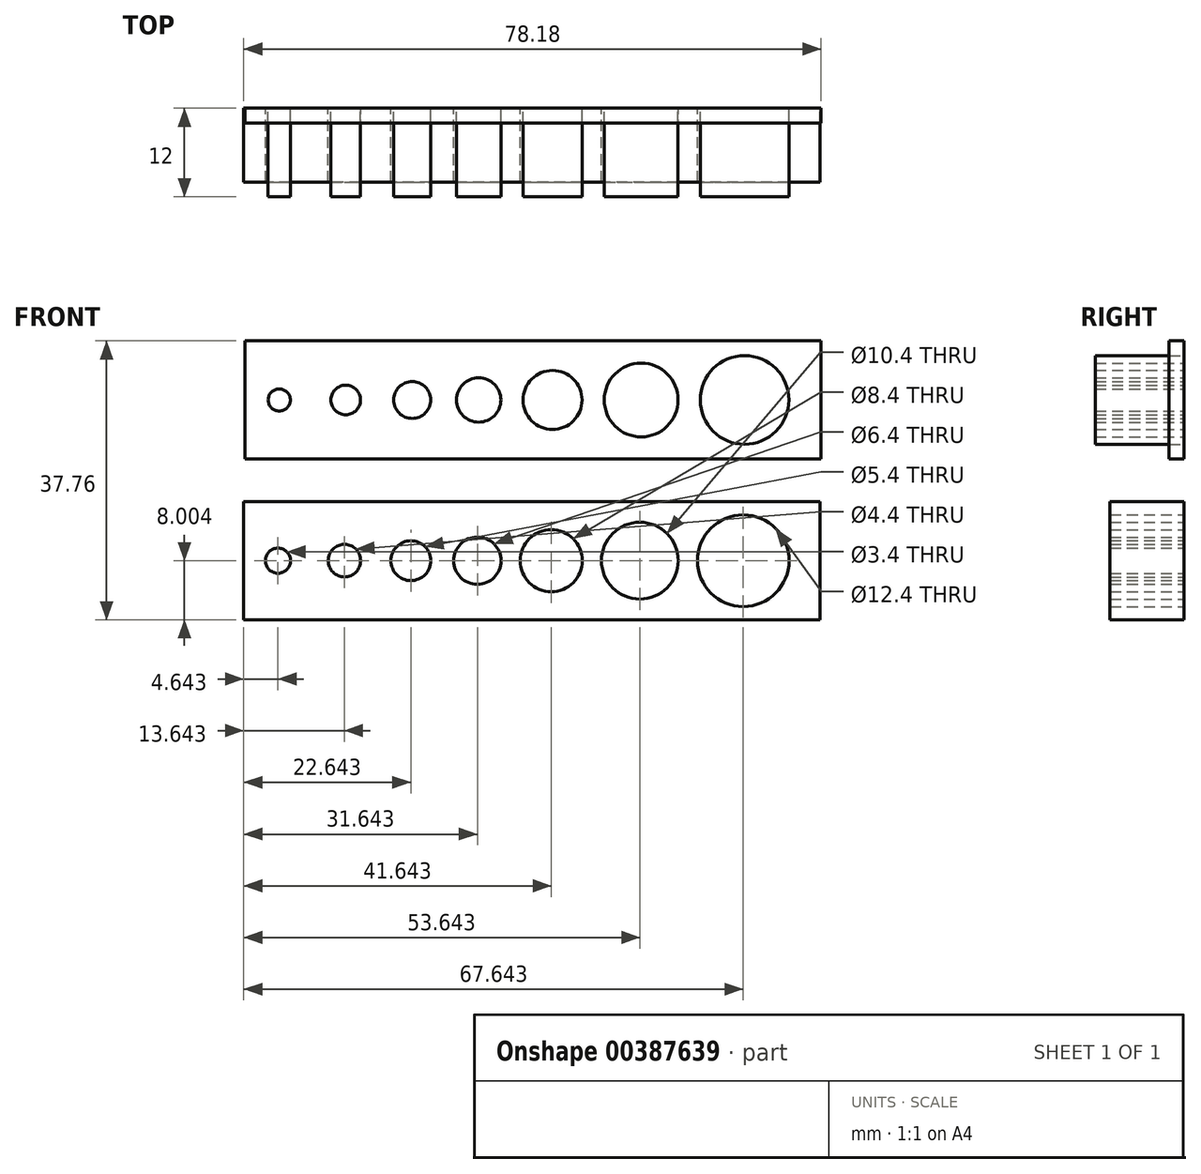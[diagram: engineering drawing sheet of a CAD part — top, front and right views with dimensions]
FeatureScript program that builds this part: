
annotation { "Feature Type Name" : "Feature", "Feature Type Description" : "" }
export const myFeature = defineFeature(function(context is Context, id is Id, definition is map)
    precondition{}
    {
        {
            var Q0;
            Q0=qCreatedBy(makeId("Front.planeOp"),FACE);
            var sketch = newSketch(context, id + "F0", { "sketchPlane" : qUnion([Q0])});
            skLineSegment(sketch, "E0", {"start": v(-39.38, 0) * mm, "end": v(47.78, 0) * mm, "construction": true});
            skCircle(sketch, "E1", {"center": v(-31.97, 0) * mm, "radius": 1.5 * mm});
            skCircle(sketch, "E2", {"center": v(-22.97, 0) * mm, "radius": 2 * mm});
            skCircle(sketch, "E3", {"center": v(-13.97, 0) * mm, "radius": 2.5 * mm});
            skCircle(sketch, "E4", {"center": v(-4.97, 0) * mm, "radius": 3 * mm});
            skCircle(sketch, "E5", {"center": v(5.03, 0) * mm, "radius": 4 * mm});
            skCircle(sketch, "E6", {"center": v(17.03, 0) * mm, "radius": 5 * mm});
            skCircle(sketch, "E7", {"center": v(31.03, 0) * mm, "radius": 6 * mm});
            skLineSegment(sketch, "E8.bottom", {"start": v(-36.6, -8) * mm, "end": v(41.4, -8) * mm});
            skLineSegment(sketch, "E8.top", {"start": v(-36.6, 8) * mm, "end": v(41.4, 8) * mm});
            skLineSegment(sketch, "E8.left", {"start": v(-36.6, -8) * mm, "end": v(-36.6, 8) * mm});
            skLineSegment(sketch, "E8.right", {"start": v(41.4, -8) * mm, "end": v(41.4, 8) * mm});
            skPoint(sketch, "E9", {"position": v(41.4, 0) * mm});
            skSolve(sketch);
        }
        {
            var Q0;
            Q0=qCreatedBy(makeId("Front.planeOp"),FACE);
            var sketch = newSketch(context, id + "F1", { "sketchPlane" : qUnion([Q0])});
            skLineSegment(sketch, "E10", {"start": v(-39.55, -21.76) * mm, "end": v(47.6, -21.76) * mm, "construction": true});
            skCircle(sketch, "E11", {"center": v(-32.15, -21.76) * mm, "radius": 1.7 * mm});
            skCircle(sketch, "E12", {"center": v(-23.15, -21.76) * mm, "radius": 2.2 * mm});
            skCircle(sketch, "E13", {"center": v(-14.15, -21.76) * mm, "radius": 2.7 * mm});
            skCircle(sketch, "E14", {"center": v(-5.15, -21.76) * mm, "radius": 3.2 * mm});
            skCircle(sketch, "E15", {"center": v(4.85, -21.76) * mm, "radius": 4.2 * mm});
            skCircle(sketch, "E16", {"center": v(16.85, -21.76) * mm, "radius": 5.2 * mm});
            skCircle(sketch, "E17", {"center": v(30.85, -21.76) * mm, "radius": 6.2 * mm});
            skLineSegment(sketch, "E18.bottom", {"start": v(-36.79, -29.76) * mm, "end": v(41.21, -29.76) * mm});
            skLineSegment(sketch, "E18.top", {"start": v(-36.79, -13.76) * mm, "end": v(41.21, -13.76) * mm});
            skLineSegment(sketch, "E18.left", {"start": v(-36.79, -29.76) * mm, "end": v(-36.79, -13.76) * mm});
            skLineSegment(sketch, "E18.right", {"start": v(41.21, -29.76) * mm, "end": v(41.21, -13.76) * mm});
            skPoint(sketch, "E19", {"position": v(41.21, -21.76) * mm});
            skSolve(sketch);
        }
        {
            var Q0;
            Q0=makeQuery(id+"F0.imprint","IMPRINT",FACE,{"disambiguationData":[TD([[makeQuery(id+"F0.imprint","IMPRINT",EDGE,{"derivedFrom":sQuery(id+"F0.wireOp",EDGE,"E3")}),1.0]])]});
            var Q1;
            Q1=makeQuery(id+"F0.imprint","IMPRINT",FACE,{"disambiguationData":[TD([[makeQuery(id+"F0.imprint","IMPRINT",EDGE,{"derivedFrom":sQuery(id+"F0.wireOp",EDGE,"E2")}),1.0]])]});
            var Q2;
            Q2=makeQuery(id+"F0.imprint","IMPRINT",FACE,{"disambiguationData":[TD([[makeQuery(id+"F0.imprint","IMPRINT",EDGE,{"derivedFrom":sQuery(id+"F0.wireOp",EDGE,"E4")}),1.0]])]});
            var Q3;
            Q3=makeQuery(id+"F0.imprint","IMPRINT",FACE,{"disambiguationData":[TD([[makeQuery(id+"F0.imprint","IMPRINT",EDGE,{"derivedFrom":sQuery(id+"F0.wireOp",EDGE,"E1")}),1.0]])]});
            var Q4;
            Q4=makeQuery(id+"F0.imprint","IMPRINT",FACE,{"disambiguationData":[TD([[makeQuery(id+"F0.imprint","IMPRINT",EDGE,{"derivedFrom":sQuery(id+"F0.wireOp",EDGE,"E5")}),1.0]])]});
            var Q5;
            Q5=makeQuery(id+"F0.imprint","IMPRINT",FACE,{"disambiguationData":[TD([[makeQuery(id+"F0.imprint","IMPRINT",EDGE,{"derivedFrom":sQuery(id+"F0.wireOp",EDGE,"E6")}),1.0]])]});
            var Q6;
            Q6=makeQuery(id+"F0.imprint","IMPRINT",FACE,{"disambiguationData":[TD([[makeQuery(id+"F0.imprint","IMPRINT",EDGE,{"derivedFrom":sQuery(id+"F0.wireOp",EDGE,"E7")}),1.0]])]});
            var Q7;
            Q7=makeQuery(id+"F0.imprint","IMPRINT",FACE,{"disambiguationData":[TD([[makeQuery(id+"F0.imprint","IMPRINT",EDGE,{"derivedFrom":sQuery(id+"F0.wireOp",EDGE,"E1")}),-1.0]])]});
            extrude(context, id + "F2", {"entities" : qUnion([Q0, Q1, Q2, Q3, Q4, Q5, Q6, Q7]), "depth" : 2 * mm});
        }
        {
            var Q0;
            Q0=makeQuery(id+"F0.imprint","IMPRINT",FACE,{"disambiguationData":[TD([[makeQuery(id+"F0.imprint","IMPRINT",EDGE,{"derivedFrom":sQuery(id+"F0.wireOp",EDGE,"E1")}),1.0]])]});
            var Q1;
            Q1=makeQuery(id+"F0.imprint","IMPRINT",FACE,{"disambiguationData":[TD([[makeQuery(id+"F0.imprint","IMPRINT",EDGE,{"derivedFrom":sQuery(id+"F0.wireOp",EDGE,"E2")}),1.0]])]});
            var Q2;
            Q2=makeQuery(id+"F0.imprint","IMPRINT",FACE,{"disambiguationData":[TD([[makeQuery(id+"F0.imprint","IMPRINT",EDGE,{"derivedFrom":sQuery(id+"F0.wireOp",EDGE,"E3")}),1.0]])]});
            var Q3;
            Q3=makeQuery(id+"F0.imprint","IMPRINT",FACE,{"disambiguationData":[TD([[makeQuery(id+"F0.imprint","IMPRINT",EDGE,{"derivedFrom":sQuery(id+"F0.wireOp",EDGE,"E4")}),1.0]])]});
            var Q4;
            Q4=makeQuery(id+"F0.imprint","IMPRINT",FACE,{"disambiguationData":[TD([[makeQuery(id+"F0.imprint","IMPRINT",EDGE,{"derivedFrom":sQuery(id+"F0.wireOp",EDGE,"E5")}),1.0]])]});
            var Q5;
            Q5=makeQuery(id+"F0.imprint","IMPRINT",FACE,{"disambiguationData":[TD([[makeQuery(id+"F0.imprint","IMPRINT",EDGE,{"derivedFrom":sQuery(id+"F0.wireOp",EDGE,"E6")}),1.0]])]});
            var Q6;
            Q6=makeQuery(id+"F0.imprint","IMPRINT",FACE,{"disambiguationData":[TD([[makeQuery(id+"F0.imprint","IMPRINT",EDGE,{"derivedFrom":sQuery(id+"F0.wireOp",EDGE,"E7")}),1.0]])]});
            extrude(context, id + "F3", {"entities" : qUnion([Q0, Q1, Q2, Q3, Q4, Q5, Q6]), "depth" : 12 * mm});
        }
        {
            var Q0;
            Q0 = qSketchRegion(id + "F1", true);
            extrude(context, id + "F4", {"entities" : qUnion([Q0]), "depth" : 10 * mm});
        }
    });
